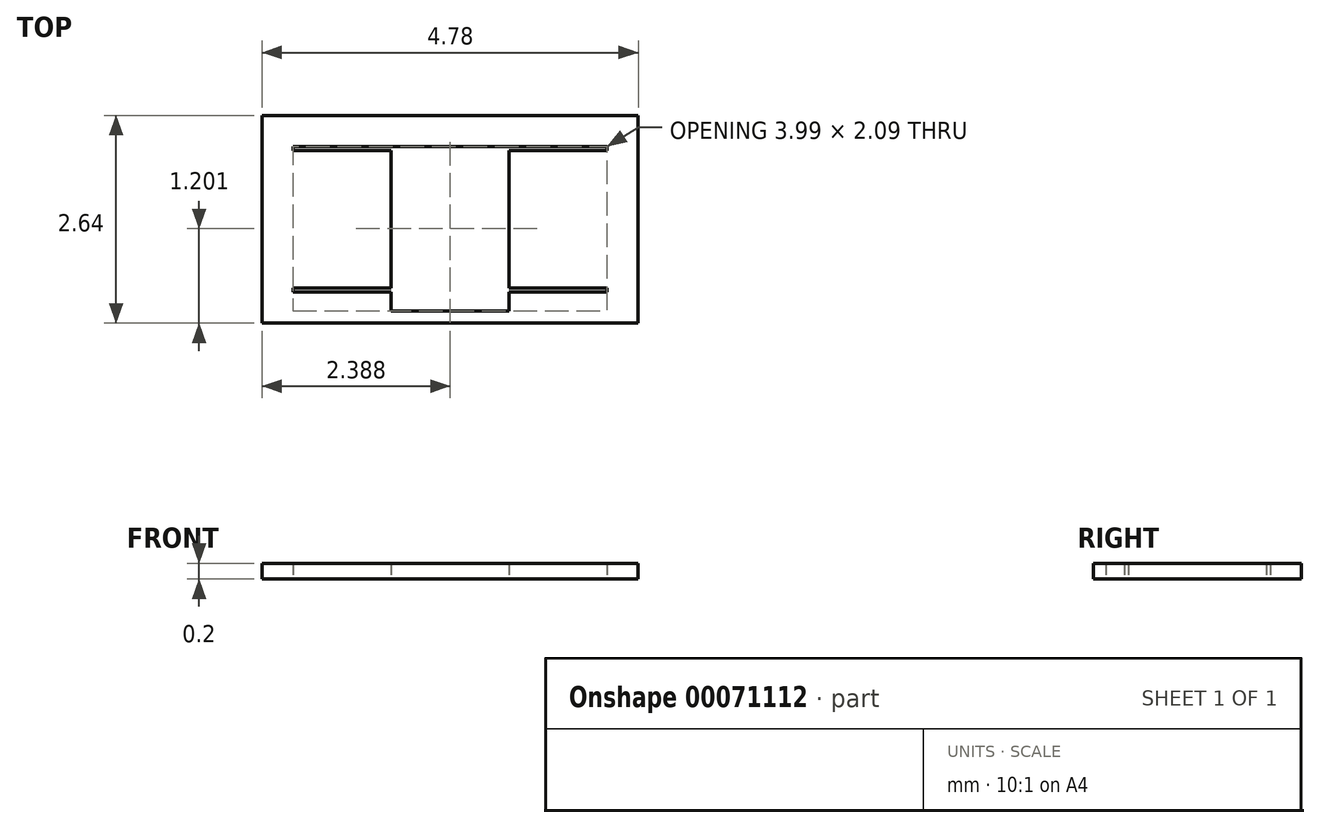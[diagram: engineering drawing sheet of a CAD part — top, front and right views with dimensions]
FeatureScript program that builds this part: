
annotation { "Feature Type Name" : "Feature", "Feature Type Description" : "" }
export const myFeature = defineFeature(function(context is Context, id is Id, definition is map)
    precondition{}
    {
        {
            var Q0;
            Q0=qCreatedBy(makeId("Top.planeOp"),FACE);
            var sketch = newSketch(context, id + "F0", { "sketchPlane" : qUnion([Q0])});
            skLineSegment(sketch, "E0", {"start": v(27.26, 1.32) * mm, "end": v(22.48, 1.32) * mm});
            skLineSegment(sketch, "E1", {"start": v(27.26, 1.32) * mm, "end": v(27.26, -1.32) * mm});
            skLineSegment(sketch, "E2", {"start": v(22.48, 1.32) * mm, "end": v(22.48, -1.32) * mm});
            skLineSegment(sketch, "E3", {"start": v(27.26, -1.32) * mm, "end": v(22.48, -1.32) * mm});
            skLineSegment(sketch, "E4", {"start": v(22.88, 0.93) * mm, "end": v(26.86, 0.93) * mm});
            skLineSegment(sketch, "E5", {"start": v(26.86, 0.93) * mm, "end": v(26.86, 0.88) * mm});
            skLineSegment(sketch, "E6", {"start": v(25.62, 0.88) * mm, "end": v(26.86, 0.88) * mm});
            skLineSegment(sketch, "E7", {"start": v(25.62, -0.88) * mm, "end": v(26.86, -0.88) * mm});
            skLineSegment(sketch, "E8", {"start": v(25.62, -0.92) * mm, "end": v(26.86, -0.92) * mm});
            skLineSegment(sketch, "E9", {"start": v(26.86, -0.88) * mm, "end": v(26.86, -0.92) * mm});
            skLineSegment(sketch, "E10", {"start": v(24.12, -0.88) * mm, "end": v(22.88, -0.88) * mm});
            skLineSegment(sketch, "E11", {"start": v(22.88, -0.88) * mm, "end": v(22.88, -0.92) * mm});
            skLineSegment(sketch, "E12", {"start": v(24.12, -0.92) * mm, "end": v(22.88, -0.92) * mm});
            skLineSegment(sketch, "E13", {"start": v(22.88, 0.93) * mm, "end": v(22.88, 0.88) * mm});
            skLineSegment(sketch, "E14", {"start": v(24.12, 0.88) * mm, "end": v(22.88, 0.88) * mm});
            skLineSegment(sketch, "E15", {"start": v(24.12, 0.88) * mm, "end": v(24.12, -0.88) * mm});
            skLineSegment(sketch, "E16", {"start": v(25.62, 0.88) * mm, "end": v(25.62, -0.88) * mm});
            skLineSegment(sketch, "E17", {"start": v(24.12, -0.92) * mm, "end": v(24.12, -1.16) * mm});
            skLineSegment(sketch, "E18", {"start": v(25.62, -1.16) * mm, "end": v(24.12, -1.16) * mm});
            skLineSegment(sketch, "E19", {"start": v(25.62, -0.92) * mm, "end": v(25.62, -1.16) * mm});
            skSolve(sketch);
        }
        {
            var Q0;
            Q0=makeQuery(id+"F0.imprint","IMPRINT",FACE,{"disambiguationData":[TD([[makeQuery(id+"F0.imprint","IMPRINT",EDGE,{"derivedFrom":sQuery(id+"F0.wireOp",EDGE,"E0")}),1.0]])]});
            extrude(context, id + "F1", {"entities" : qUnion([Q0]), "depth" : .2 * mm});
        }
    });
